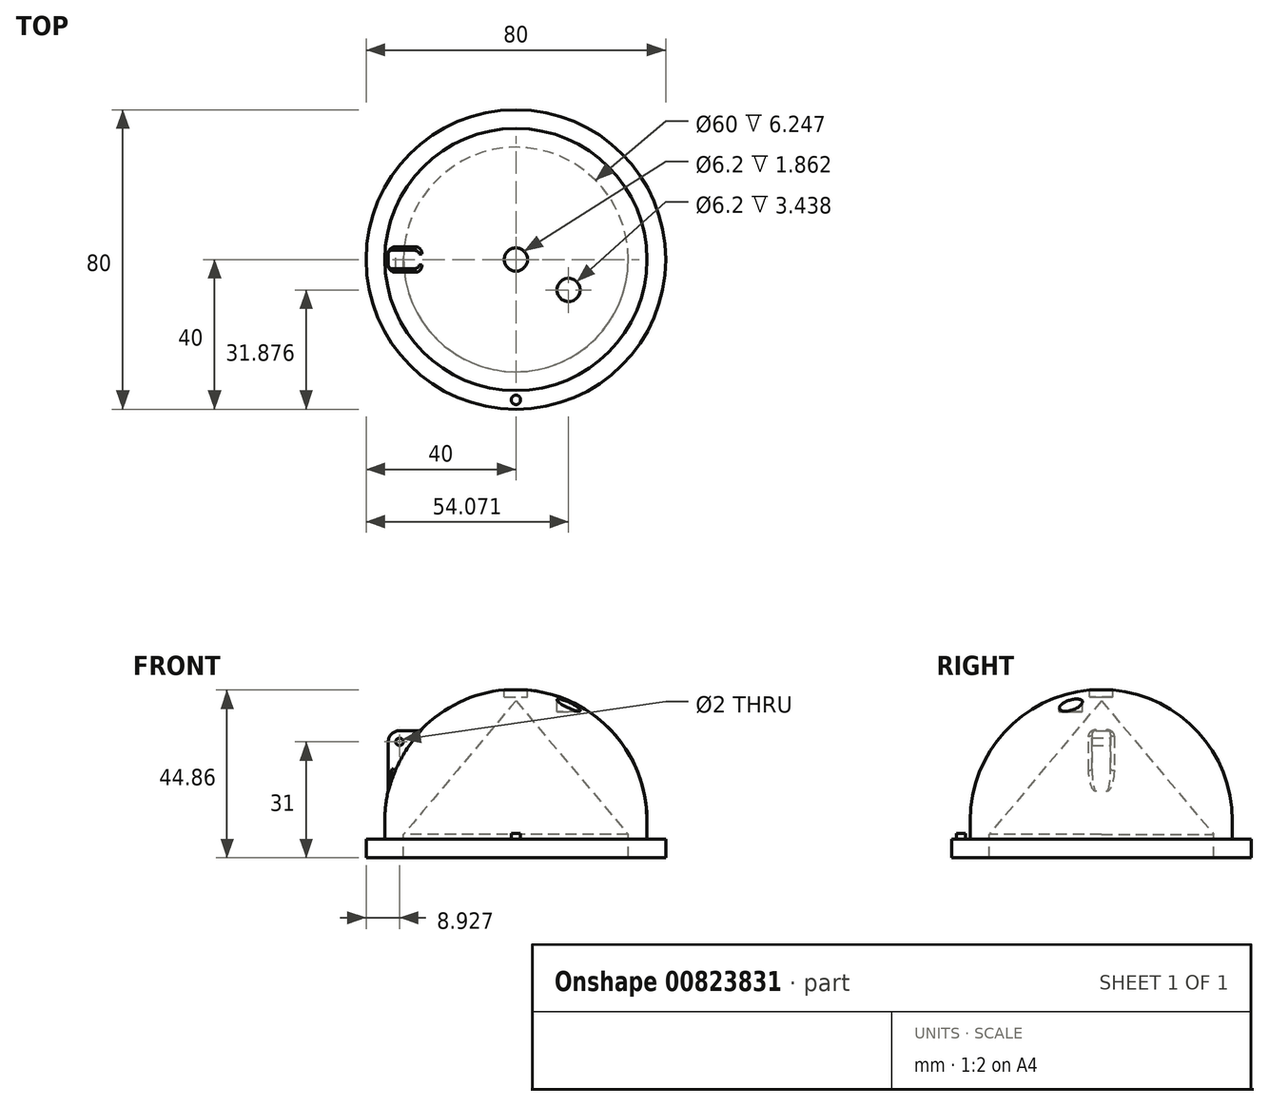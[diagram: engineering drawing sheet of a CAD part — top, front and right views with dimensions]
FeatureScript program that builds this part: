
annotation { "Feature Type Name" : "Feature", "Feature Type Description" : "" }
export const myFeature = defineFeature(function(context is Context, id is Id, definition is map)
    precondition{}
    {
        {
            var Q0;
            Q0=qCreatedBy(makeId("Front.planeOp"),FACE);
            var sketch = newSketch(context, id + "F0", { "sketchPlane" : qUnion([Q0])});
            skLineSegment(sketch, "E0", {"start": v(30, 0) * mm, "end": v(40, 0) * mm});
            skArc(sketch, "E1", {"start": v(35, 10) * mm, "mid": v(24.75, 34.75) * mm, "end": v(0, 45) * mm});
            skLineSegment(sketch, "E2", {"start": v(0, 45) * mm, "end": v(0, 10) * mm});
            skLineSegment(sketch, "E3", {"start": v(35, 10) * mm, "end": v(35, 5) * mm});
            skLineSegment(sketch, "E4", {"start": v(35, 5) * mm, "end": v(40, 5) * mm});
            skLineSegment(sketch, "E5", {"start": v(40, 5) * mm, "end": v(40, 0) * mm});
            skLineSegment(sketch, "E6", {"start": v(30, 6.25) * mm, "end": v(30, 0) * mm});
            skLineSegment(sketch, "E7", {"start": v(0, 10) * mm, "end": v(35, 10) * mm, "construction": true});
            skLineSegment(sketch, "E8", {"start": v(0, 42) * mm, "end": v(0, 10) * mm, "construction": true});
            skLineSegment(sketch, "E9", {"start": v(0, 42) * mm, "end": v(0, 42) * mm});
            skLineSegment(sketch, "E10", {"start": v(0, 42) * mm, "end": v(30, 6.25) * mm});
            skSolve(sketch);
        }
        {
            var Q0;
            Q0=makeQuery(id+"F0.imprint","IMPRINT",FACE,{"disambiguationData":[TD([[makeQuery(id+"F0.imprint","IMPRINT",EDGE,{"derivedFrom":sQuery(id+"F0.wireOp",EDGE,"E0")}),1.0]])]});
            var Q1;
            Q1=sQuery(id+"F0.wireOp",EDGE,"E2");
            revolve(context, id + "F1", {"surfaceOperationType" : NewSurfaceOperationType.NEW, "entities" : qUnion([Q0]), "axis" : qUnion([Q1]), "revolveType" : RevolveType.FULL});
        }
        {
            var Q0;
            Q0=makeQuery(id+"F1.opRevolve","SWEPT_FACE",FACE,{"disambiguationData":[OSD([sQuery(id+"F0.wireOp",EDGE,"E4")])]});
            var sketch = newSketch(context, id + "F2", { "sketchPlane" : qUnion([Q0])});
            skCircle(sketch, "E11", {"center": v(0, 0) * mm, "radius": 37.5 * mm, "construction": true});
            skPoint(sketch, "E12", {"position": v(0, -37.5) * mm});
            skCircle(sketch, "E13", {"center": v(0, -37.5) * mm, "radius": 1.25 * mm});
            skSolve(sketch);
        }
        {
            var Q0;
            Q0=makeQuery(id+"F2.imprint","IMPRINT",FACE,{"disambiguationData":[TD([[makeQuery(id+"F2.imprint","IMPRINT",EDGE,{"derivedFrom":sQuery(id+"F2.wireOp",EDGE,"28ad08c0-a5c5-41d9-acc3-98da09d5684a.0")}),-1.0]])]});
            var Q1;
            Q1=makeQuery(id+"F2.imprint","IMPRINT",FACE,{"disambiguationData":[TD([[makeQuery(id+"F2.imprint","IMPRINT",EDGE,{"derivedFrom":sQuery(id+"F2.wireOp",EDGE,"E13")}),1.0]])]});
            extrude(context, id + "F3", {"entities" : qUnion([Q0, Q1]), "operationType" : NewBodyOperationType.ADD, "depth" : 1.5 * mm, "offsetDistance" : 25 * mm});
        }
        {
            var Q0;
            Q0=makeQuery(id+"F1.opRevolve","SWEPT_EDGE",EDGE,{"disambiguationData":[OSD([sQuery(id+"F0.wireOp",EDGE,"E3"),sQuery(id+"F0.wireOp",EDGE,"E4")])]});
            fillet(context, id + "F4", {"entities" : qUnion([Q0]), "radius" : .5 * mm, "tangentPropagation" : true, "allowEdgeOverflow" : false});
        }
        {
            var Q0;
            Q0=sQuery(id+"F0.wireOp",EDGE,"E2");
            var Q1;
            Q1=sQuery(id+"F0.wireOp",VERTEX,"E1.end");
            cPlane(context, id + "F5", {"entities" : qUnion([Q0, Q1]), "cplaneType" : CPlaneType.LINE_POINT, "offset" : 25 * mm, "width" : 150 * mm, "height" : 150 * mm});
        }
        {
            var Q0;
            Q0=qCreatedBy(id+"F5.planeOp",FACE);
            var sketch = newSketch(context, id + "F6", { "sketchPlane" : qUnion([Q0])});
            skCircle(sketch, "E14", {"center": v(0, 0) * mm, "radius": 3.1 * mm});
            skSolve(sketch);
        }
        {
            var Q0;
            Q0 = qSketchRegion(id + "F6", true);
            extrude(context, id + "F7", {"entities" : qUnion([Q0]), "operationType" : NewBodyOperationType.REMOVE, "depth" : 2 * mm, "offsetDistance" : 25 * mm});
        }
        {
            var Q0;
            Q0=qCreatedBy(makeId("Front.planeOp"),FACE);
            var sketch = newSketch(context, id + "F8", { "sketchPlane" : qUnion([Q0])});
            skArc(sketch, "E15", {"start": v(-25.48, 34) * mm, "mid": v(-30.83, 26.57) * mm, "end": v(-34.07, 18) * mm, "construction": true});
            skLineSegment(sketch, "E16", {"start": v(-34.07, 18) * mm, "end": v(-34.07, 31) * mm});
            skLineSegment(sketch, "E17", {"start": v(-25.48, 34) * mm, "end": v(-31.07, 34) * mm});
            skArc(sketch, "E18", {"start": v(-31.07, 34) * mm, "mid": v(-33.2, 33.12) * mm, "end": v(-34.07, 31) * mm});
            skCircle(sketch, "E19", {"center": v(-31.07, 31) * mm, "radius": 1 * mm});
            skLineSegment(sketch, "E20", {"start": v(-25.48, 34) * mm, "end": v(-23.48, 34) * mm});
            skLineSegment(sketch, "E21", {"start": v(-23.48, 34) * mm, "end": v(-34.07, 15) * mm});
            skLineSegment(sketch, "E22", {"start": v(-34.07, 15) * mm, "end": v(-34.07, 18) * mm});
            skSolve(sketch);
        }
        {
            var Q0;
            Q0=qCreatedBy(id+"F5.planeOp",FACE);
            cPlane(context, id + "F9", {"entities" : qUnion([Q0]), "cplaneType" : CPlaneType.OFFSET, "offset" : 4 * mm, "width" : 150 * mm, "height" : 150 * mm});
        }
        {
            var Q0;
            Q0=qCreatedBy(id+"F9.planeOp",FACE);
            var sketch = newSketch(context, id + "F10", { "sketchPlane" : qUnion([Q0])});
            skLineSegment(sketch, "E23.0", {"start": v(35, 0) * mm, "end": v(0, 0) * mm, "construction": true});
            skSolve(sketch);
        }
        {
            var Q0;
            Q0=qCreatedBy(makeId("Front.planeOp"),FACE);
            var sketch = newSketch(context, id + "F11", { "sketchPlane" : qUnion([Q0])});
            skArc(sketch, "E24", {"start": v(-1.67, 44.96) * mm, "mid": v(0, -25) * mm, "end": v(1.67, 44.96) * mm, "construction": true});
            skLineSegment(sketch, "E25.0", {"start": v(35, 41) * mm, "end": v(0, 41) * mm, "construction": true});
            skPoint(sketch, "E26", {"position": v(16.25, 41) * mm});
            skSolve(sketch);
        }
        {
            var Q0;
            Q0=qCreatedBy(id+"F9.planeOp",FACE);
            var sketch = newSketch(context, id + "F12", { "sketchPlane" : qUnion([Q0])});
            skPoint(sketch, "E27.0", {"position": v(16.25, 0) * mm});
            skCircle(sketch, "E28", {"center": v(0, 0) * mm, "radius": 16.25 * mm, "construction": true});
            skLineSegment(sketch, "E29", {"start": v(0, 0) * mm, "end": v(14.07, 8.12) * mm, "construction": true});
            skCircle(sketch, "E30", {"center": v(14.07, 8.12) * mm, "radius": 3.1 * mm});
            skSolve(sketch);
        }
        {
            var Q0;
            Q0 = qSketchRegion(id + "F12", true);
            extrude(context, id + "F13", {"entities" : qUnion([Q0]), "operationType" : NewBodyOperationType.REMOVE, "depth" : 4 * mm, "offsetDistance" : 25 * mm, "symmetric" : true});
        }
        {
            var Q0;
            Q0=makeQuery(id+"F8.imprint","IMPRINT",FACE,{"disambiguationData":[TD([[makeQuery(id+"F8.imprint","IMPRINT",EDGE,{"derivedFrom":sQuery(id+"F8.wireOp",EDGE,"E16")}),-1.0]])]});
            extrude(context, id + "F14", {"entities" : qUnion([Q0]), "operationType" : NewBodyOperationType.ADD, "depth" : 5 * mm, "offsetDistance" : 25 * mm, "symmetric" : true});
        }
        {
            var Q0;
            Q0=makeQuery(id+"F14.boolean.opBoolean","INTERSECT",EDGE,{"derivedFrom":[makeQuery(id+"F1.opRevolve","SWEPT_FACE",FACE,{"disambiguationData":[OSD([sQuery(id+"F0.wireOp",EDGE,"E1")])]}),makeQuery(id+"F14.opExtrude","SWEPT_FACE",FACE,{"disambiguationData":[OSD([sQuery(id+"F8.wireOp",EDGE,"E16"),sQuery(id+"F8.wireOp",EDGE,"E22")])]})]});
            var Q1;
            Q1=makeQuery(id+"F14.boolean.opBoolean","INTERSECT",EDGE,{"derivedFrom":[makeQuery(id+"F1.opRevolve","SWEPT_FACE",FACE,{"disambiguationData":[OSD([sQuery(id+"F0.wireOp",EDGE,"E1")])]}),makeQuery(id+"F14.opExtrude","CAP_FACE",FACE,{"disambiguationData":[OSD([sQuery(id+"F8.wireOp",EDGE,"E16"),sQuery(id+"F8.wireOp",EDGE,"E17"),sQuery(id+"F8.wireOp",EDGE,"E18"),sQuery(id+"F8.wireOp",EDGE,"E19"),sQuery(id+"F8.wireOp",EDGE,"E20"),sQuery(id+"F8.wireOp",EDGE,"E21"),sQuery(id+"F8.wireOp",EDGE,"E22")])],"isStart":false})]});
            var Q2;
            Q2=makeQuery(id+"F14.opExtrude","CAP_EDGE",EDGE,{"disambiguationData":[OSD([sQuery(id+"F8.wireOp",EDGE,"E16"),sQuery(id+"F8.wireOp",EDGE,"E22")])],"isStart":false});
            var Q3;
            Q3=makeQuery(id+"F14.opExtrude","CAP_EDGE",EDGE,{"disambiguationData":[OSD([sQuery(id+"F8.wireOp",EDGE,"E17"),sQuery(id+"F8.wireOp",EDGE,"E20")])],"isStart":false});
            var Q4;
            Q4=makeQuery(id+"F14.opExtrude","CAP_EDGE",EDGE,{"disambiguationData":[OSD([sQuery(id+"F8.wireOp",EDGE,"E18")])],"isStart":false});
            var Q5;
            Q5=makeQuery(id+"F14.opExtrude","CAP_EDGE",EDGE,{"disambiguationData":[OSD([sQuery(id+"F8.wireOp",EDGE,"E18")])],"isStart":true});
            var Q6;
            Q6=makeQuery(id+"F14.opExtrude","CAP_EDGE",EDGE,{"disambiguationData":[OSD([sQuery(id+"F8.wireOp",EDGE,"E16"),sQuery(id+"F8.wireOp",EDGE,"E22")])],"isStart":true});
            var Q7;
            Q7=makeQuery(id+"F14.boolean.opBoolean","INTERSECT",EDGE,{"derivedFrom":[makeQuery(id+"F1.opRevolve","SWEPT_FACE",FACE,{"disambiguationData":[OSD([sQuery(id+"F0.wireOp",EDGE,"E1")])]}),makeQuery(id+"F14.opExtrude","CAP_FACE",FACE,{"disambiguationData":[OSD([sQuery(id+"F8.wireOp",EDGE,"E16"),sQuery(id+"F8.wireOp",EDGE,"E17"),sQuery(id+"F8.wireOp",EDGE,"E18"),sQuery(id+"F8.wireOp",EDGE,"E19"),sQuery(id+"F8.wireOp",EDGE,"E20"),sQuery(id+"F8.wireOp",EDGE,"E21"),sQuery(id+"F8.wireOp",EDGE,"E22")])],"isStart":true})]});
            var Q8;
            Q8=makeQuery(id+"F14.opExtrude","CAP_EDGE",EDGE,{"disambiguationData":[OSD([sQuery(id+"F8.wireOp",EDGE,"E17"),sQuery(id+"F8.wireOp",EDGE,"E20")])],"isStart":true});
            var Q9;
            Q9=makeQuery(id+"F14.boolean.opBoolean","INTERSECT",EDGE,{"derivedFrom":[makeQuery(id+"F1.opRevolve","SWEPT_FACE",FACE,{"disambiguationData":[OSD([sQuery(id+"F0.wireOp",EDGE,"E1")])]}),makeQuery(id+"F14.opExtrude","SWEPT_FACE",FACE,{"disambiguationData":[OSD([sQuery(id+"F8.wireOp",EDGE,"E17"),sQuery(id+"F8.wireOp",EDGE,"E20")])]})]});
            fillet(context, id + "F15", {"entities" : qUnion([Q0, Q1, Q2, Q3, Q4, Q5, Q6, Q7, Q8, Q9]), "radius" : 1 * mm, "tangentPropagation" : true, "allowEdgeOverflow" : false});
        }
    });
